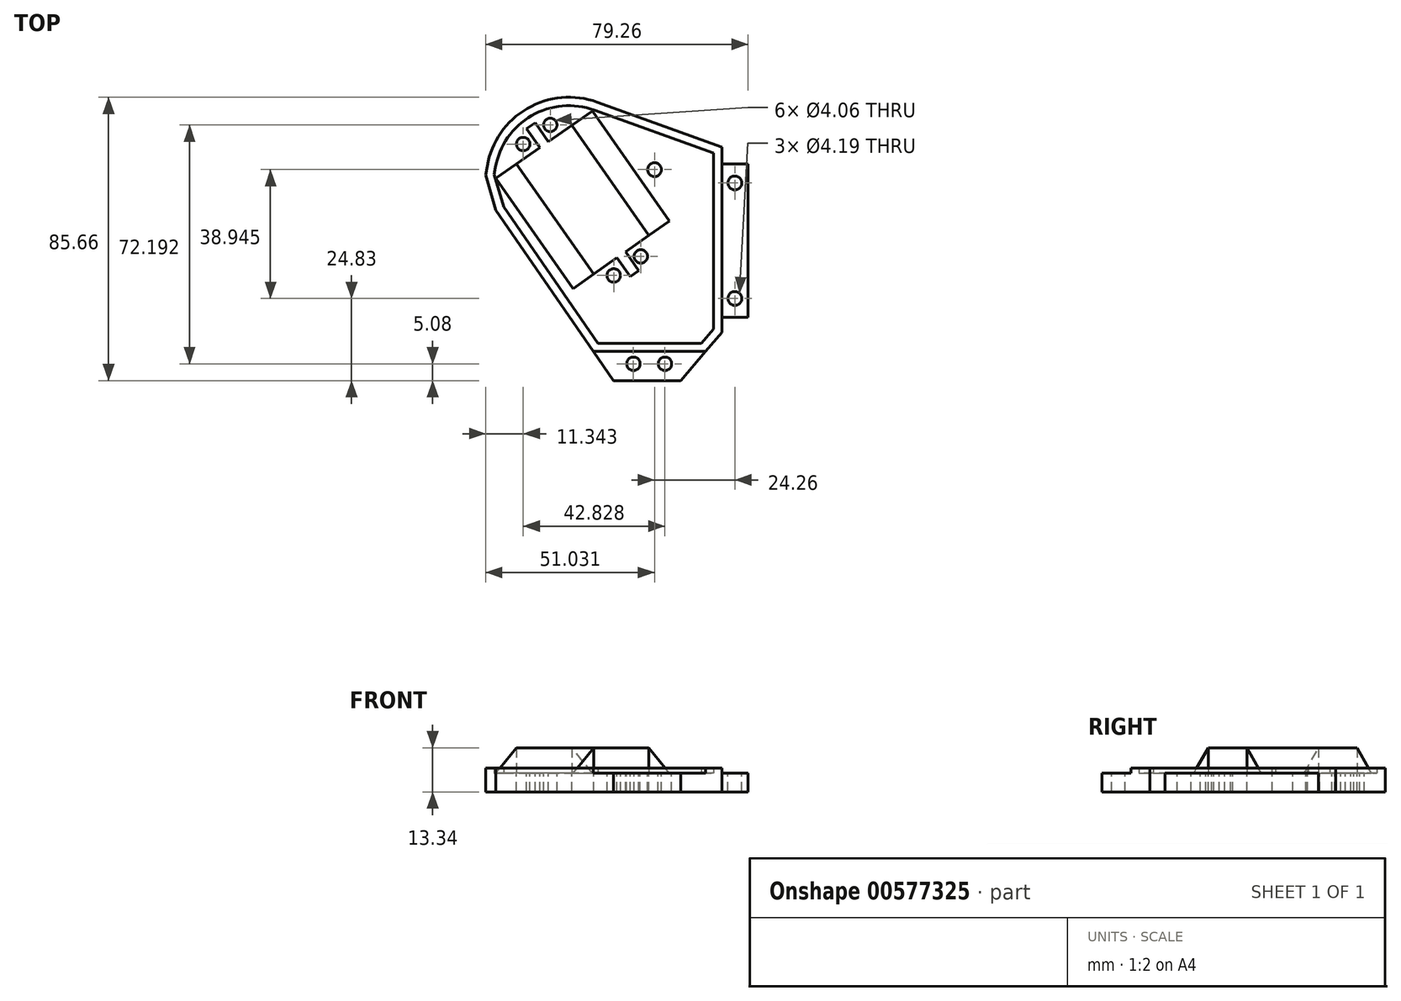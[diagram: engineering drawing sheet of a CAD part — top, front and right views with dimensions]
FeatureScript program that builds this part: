
annotation { "Feature Type Name" : "Feature", "Feature Type Description" : "" }
export const myFeature = defineFeature(function(context is Context, id is Id, definition is map)
    precondition{}
    {
        {
            var Q0;
            Q0=qCreatedBy(makeId("Top.planeOp"),FACE);
            var sketch = newSketch(context, id + "F0", { "sketchPlane" : qUnion([Q0])});
            skLineSegment(sketch, "E0", {"start": v(-30.33, 22.6) * mm, "end": v(-7.02, -10.68) * mm});
            skLineSegment(sketch, "E1", {"start": v(-7.02, -10.68) * mm, "end": v(0, -5.77) * mm});
            skLineSegment(sketch, "E2", {"start": v(9.62, 0.97) * mm, "end": v(-13.69, 34.26) * mm});
            skLineSegment(sketch, "E3", {"start": v(-13.69, 34.26) * mm, "end": v(-20.7, 29.35) * mm});
            skLineSegment(sketch, "E4", {"start": v(-20.7, 29.35) * mm, "end": v(-24.72, 35.07) * mm});
            skLineSegment(sketch, "E5", {"start": v(-24.72, 35.07) * mm, "end": v(-27.32, 33.25) * mm});
            skLineSegment(sketch, "E6", {"start": v(-27.32, 33.25) * mm, "end": v(-23.31, 27.52) * mm});
            skLineSegment(sketch, "E7", {"start": v(0, -5.77) * mm, "end": v(4, -11.49) * mm});
            skLineSegment(sketch, "E8", {"start": v(4, -11.49) * mm, "end": v(6.6, -9.67) * mm});
            skLineSegment(sketch, "E9", {"start": v(6.6, -9.67) * mm, "end": v(2.6, -3.95) * mm});
            skArc(sketch, "E10", {"start": v(-5.96, 41.3) * mm, "mid": v(-27.09, 39.38) * mm, "end": v(-39.21, 21.97) * mm});
            skLineSegment(sketch, "E11", {"start": v(-36.58, 8.59) * mm, "end": v(-1.1, -42.88) * mm});
            skLineSegment(sketch, "E12", {"start": v(-1.1, -42.88) * mm, "end": v(19.25, -42.88) * mm});
            skLineSegment(sketch, "E13", {"start": v(19.25, -42.88) * mm, "end": v(31.65, -28.3) * mm});
            skLineSegment(sketch, "E14", {"start": v(31.65, -28.3) * mm, "end": v(31.65, -23.76) * mm});
            skLineSegment(sketch, "E15", {"start": v(31.65, -23.76) * mm, "end": v(39.59, -23.76) * mm});
            skLineSegment(sketch, "E16", {"start": v(39.59, -23.76) * mm, "end": v(39.59, 22.6) * mm});
            skLineSegment(sketch, "E17", {"start": v(39.59, 22.6) * mm, "end": v(31.65, 22.6) * mm});
            skLineSegment(sketch, "E18", {"start": v(31.65, 22.6) * mm, "end": v(31.65, 27.74) * mm});
            skLineSegment(sketch, "E19", {"start": v(31.65, 27.74) * mm, "end": v(-5.96, 41.3) * mm});
            skLineSegment(sketch, "E20", {"start": v(-36.58, 8.59) * mm, "end": v(-39.67, 19.34) * mm});
            skLineSegment(sketch, "E21", {"start": v(-39.67, 19.34) * mm, "end": v(-39.21, 21.97) * mm});
            skLineSegment(sketch, "E22", {"start": v(-31.64, 42.2) * mm, "end": v(10.17, -17.52) * mm, "construction": true});
            skLineSegment(sketch, "E23.trimOffspring", {"start": v(-23.31, 27.52) * mm, "end": v(-30.33, 22.6) * mm});
            skLineSegment(sketch, "E24.trimOffspring", {"start": v(2.6, -3.95) * mm, "end": v(9.62, 0.97) * mm});
            skCircle(sketch, "E25", {"center": v(35.62, 16.88) * mm, "radius": 2.1 * mm});
            skPoint(sketch, "E25.centerSnap0", {"position": v(35.62, 22.6) * mm});
            skCircle(sketch, "E26", {"center": v(35.62, -18.05) * mm, "radius": 2.1 * mm});
            skPoint(sketch, "E26.centerSnap0", {"position": v(35.62, -23.76) * mm});
            skCircle(sketch, "E27", {"center": v(4.98, -37.8) * mm, "radius": 2.03 * mm});
            skCircle(sketch, "E28", {"center": v(14.5, -37.8) * mm, "radius": 2.03 * mm});
            skCircle(sketch, "E29", {"center": v(11.36, 20.9) * mm, "radius": 2.1 * mm});
            skCircle(sketch, "E30", {"center": v(-20.14, 34.4) * mm, "radius": 2.03 * mm});
            skCircle(sketch, "E31", {"center": v(-28.33, 28.63) * mm, "radius": 2.03 * mm});
            skCircle(sketch, "E32", {"center": v(7.2, -5.34) * mm, "radius": 2.03 * mm});
            skCircle(sketch, "E33", {"center": v(-0.98, -11.1) * mm, "radius": 2.03 * mm});
            skSolve(sketch);
        }
        {
            var Q0;
            Q0=makeQuery(id+"F0.imprint","IMPRINT",FACE,{"disambiguationData":[TD([[makeQuery(id+"F0.imprint","IMPRINT",EDGE,{"derivedFrom":sQuery(id+"F0.wireOp",EDGE,"E0")}),-1.0]])]});
            extrude(context, id + "F1", {"entities" : qUnion([Q0]), "oppositeDirection" : true, "depth" : 5.7 * mm, "offsetDistance" : 25.4 * mm});
        }
        {
            var Q0;
            Q0=makeQuery(id+"F1.opExtrude","CAP_FACE",FACE,{"disambiguationData":[OSD([sQuery(id+"F0.wireOp",EDGE,"E0"),sQuery(id+"F0.wireOp",EDGE,"E1"),sQuery(id+"F0.wireOp",EDGE,"E2"),sQuery(id+"F0.wireOp",EDGE,"E3"),sQuery(id+"F0.wireOp",EDGE,"E4"),sQuery(id+"F0.wireOp",EDGE,"E5"),sQuery(id+"F0.wireOp",EDGE,"E6"),sQuery(id+"F0.wireOp",EDGE,"E7"),sQuery(id+"F0.wireOp",EDGE,"E8"),sQuery(id+"F0.wireOp",EDGE,"E9"),sQuery(id+"F0.wireOp",EDGE,"E10"),sQuery(id+"F0.wireOp",EDGE,"E11"),sQuery(id+"F0.wireOp",EDGE,"E12"),sQuery(id+"F0.wireOp",EDGE,"E13"),sQuery(id+"F0.wireOp",EDGE,"E14"),sQuery(id+"F0.wireOp",EDGE,"E15"),sQuery(id+"F0.wireOp",EDGE,"E16"),sQuery(id+"F0.wireOp",EDGE,"E17"),sQuery(id+"F0.wireOp",EDGE,"E18"),sQuery(id+"F0.wireOp",EDGE,"E19"),sQuery(id+"F0.wireOp",EDGE,"E20"),sQuery(id+"F0.wireOp",EDGE,"E21"),sQuery(id+"F0.wireOp",EDGE,"E23.trimOffspring"),sQuery(id+"F0.wireOp",EDGE,"E24.trimOffspring"),sQuery(id+"F0.wireOp",EDGE,"E25"),sQuery(id+"F0.wireOp",EDGE,"E26"),sQuery(id+"F0.wireOp",EDGE,"E27"),sQuery(id+"F0.wireOp",EDGE,"E28"),sQuery(id+"F0.wireOp",EDGE,"E29"),sQuery(id+"F0.wireOp",EDGE,"E30"),sQuery(id+"F0.wireOp",EDGE,"E31"),sQuery(id+"F0.wireOp",EDGE,"E32"),sQuery(id+"F0.wireOp",EDGE,"E33")])],"isStart":true});
            var sketch = newSketch(context, id + "F2", { "sketchPlane" : qUnion([Q0])});
            skLineSegment(sketch, "E34.0.0", {"start": v(39.59, -23.76) * mm, "end": v(39.59, 22.6) * mm});
            skLineSegment(sketch, "E34.0.1", {"start": v(39.59, 22.6) * mm, "end": v(31.65, 22.6) * mm});
            skLineSegment(sketch, "E34.0.2", {"start": v(31.65, 22.6) * mm, "end": v(31.65, 27.74) * mm});
            skLineSegment(sketch, "E34.0.3", {"start": v(31.65, 27.74) * mm, "end": v(-5.96, 41.3) * mm});
            skArc(sketch, "E34.0.4", {"start": v(-5.96, 41.3) * mm, "mid": v(-27.09, 39.38) * mm, "end": v(-39.21, 21.97) * mm});
            skLineSegment(sketch, "E34.0.5", {"start": v(-39.21, 21.97) * mm, "end": v(-39.67, 19.34) * mm});
            skLineSegment(sketch, "E34.0.6", {"start": v(-39.67, 19.34) * mm, "end": v(-36.58, 8.59) * mm});
            skLineSegment(sketch, "E34.0.7", {"start": v(-36.58, 8.59) * mm, "end": v(-1.1, -42.88) * mm});
            skLineSegment(sketch, "E34.0.8", {"start": v(-1.1, -42.88) * mm, "end": v(19.25, -42.88) * mm});
            skLineSegment(sketch, "E34.0.9", {"start": v(19.25, -42.88) * mm, "end": v(31.65, -28.3) * mm});
            skLineSegment(sketch, "E34.0.10", {"start": v(31.65, -28.3) * mm, "end": v(31.65, -23.76) * mm});
            skLineSegment(sketch, "E34.0.11", {"start": v(31.65, -23.76) * mm, "end": v(39.59, -23.76) * mm});
            skLineSegment(sketch, "E35", {"start": v(31.65, 22.6) * mm, "end": v(31.65, -23.76) * mm});
            skLineSegment(sketch, "E36.0", {"start": v(29.11, 22.6) * mm, "end": v(29.11, 25.96) * mm});
            skLineSegment(sketch, "E36.1", {"start": v(29.11, 22.6) * mm, "end": v(29.11, -23.76) * mm});
            skLineSegment(sketch, "E36.2", {"start": v(29.11, 25.96) * mm, "end": v(-6.82, 38.9) * mm});
            skLineSegment(sketch, "E36.3", {"start": v(29.11, -27.36) * mm, "end": v(29.11, -23.76) * mm});
            skLineSegment(sketch, "E36.4", {"start": v(25.52, -31.59) * mm, "end": v(29.11, -27.36) * mm});
            skArc(sketch, "E36.6", {"start": v(-6.82, 38.9) * mm, "mid": v(-25.81, 37.19) * mm, "end": v(-36.71, 21.54) * mm});
            skLineSegment(sketch, "E36.7", {"start": v(-36.71, 21.54) * mm, "end": v(-37.07, 19.48) * mm});
            skLineSegment(sketch, "E36.8", {"start": v(-37.07, 19.48) * mm, "end": v(-34.26, 9.69) * mm});
            skLineSegment(sketch, "E36.9", {"start": v(-34.26, 9.69) * mm, "end": v(-5.8, -31.59) * mm});
            skLineSegment(sketch, "E37", {"start": v(-7.2, -34.02) * mm, "end": v(26.78, -34.02) * mm});
            skLineSegment(sketch, "E38", {"start": v(-5.8, -31.59) * mm, "end": v(25.52, -31.59) * mm});
            skSolve(sketch);
        }
        {
            var Q0;
            Q0=makeQuery(id+"F2.imprint","IMPRINT",FACE,{"disambiguationData":[TD([[makeQuery(id+"F2.imprint","IMPRINT",EDGE,{"derivedFrom":sQuery(id+"F2.wireOp",EDGE,"E34.0.2")}),1.0]])]});
            extrude(context, id + "F3", {"entities" : qUnion([Q0]), "operationType" : NewBodyOperationType.ADD, "depth" : 1.52 * mm, "offsetDistance" : 25.4 * mm});
        }
        {
            var Q0;
            Q0=makeQuery(id+"F1.opExtrude","SWEPT_FACE",FACE,{"disambiguationData":[OSD([sQuery(id+"F0.wireOp",EDGE,"E23.trimOffspring")])]});
            var sketch = newSketch(context, id + "F4", { "sketchPlane" : qUnion([Q0])});
            skPoint(sketch, "E39.0", {"position": v(8.44, 0) * mm});
            skLineSegment(sketch, "E40", {"start": v(-11.88, 0) * mm, "end": v(-19.5, 0) * mm});
            skLineSegment(sketch, "E41", {"start": v(-19.5, 0) * mm, "end": v(-11.88, 7.62) * mm});
            skLineSegment(sketch, "E42", {"start": v(-11.88, 7.62) * mm, "end": v(-11.88, 0) * mm});
            skLineSegment(sketch, "E43", {"start": v(8.44, 0) * mm, "end": v(16.06, 0) * mm});
            skLineSegment(sketch, "E44", {"start": v(16.06, 0) * mm, "end": v(8.44, 7.62) * mm});
            skLineSegment(sketch, "E45", {"start": v(8.44, 7.62) * mm, "end": v(8.44, 0) * mm});
            skSolve(sketch);
        }
        {
            var Q0;
            Q0=makeQuery(id+"F4.imprint","IMPRINT",FACE,{"disambiguationData":[TD([[makeQuery(id+"F4.imprint","IMPRINT",EDGE,{"derivedFrom":sQuery(id+"F4.wireOp",EDGE,"E40")}),-1.0]])]});
            var Q1;
            Q1=makeQuery(id+"F4.imprint","IMPRINT",FACE,{"disambiguationData":[TD([[makeQuery(id+"F4.imprint","IMPRINT",EDGE,{"derivedFrom":sQuery(id+"F4.wireOp",EDGE,"E43")}),1.0]])]});
            var Q2;
            Q2=makeQuery(id+"F1.opExtrude","SWEPT_FACE",FACE,{"disambiguationData":[OSD([sQuery(id+"F0.wireOp",EDGE,"E24.trimOffspring")])]});
            extrude(context, id + "F5", {"entities" : qUnion([Q0, Q1]), "operationType" : NewBodyOperationType.ADD, "endBound" : BoundingType.UP_TO_SURFACE, "depth" : 25.4 * mm, "endBoundEntityFace" : qUnion([Q2]), "offsetDistance" : 25.4 * mm});
        }
    });
